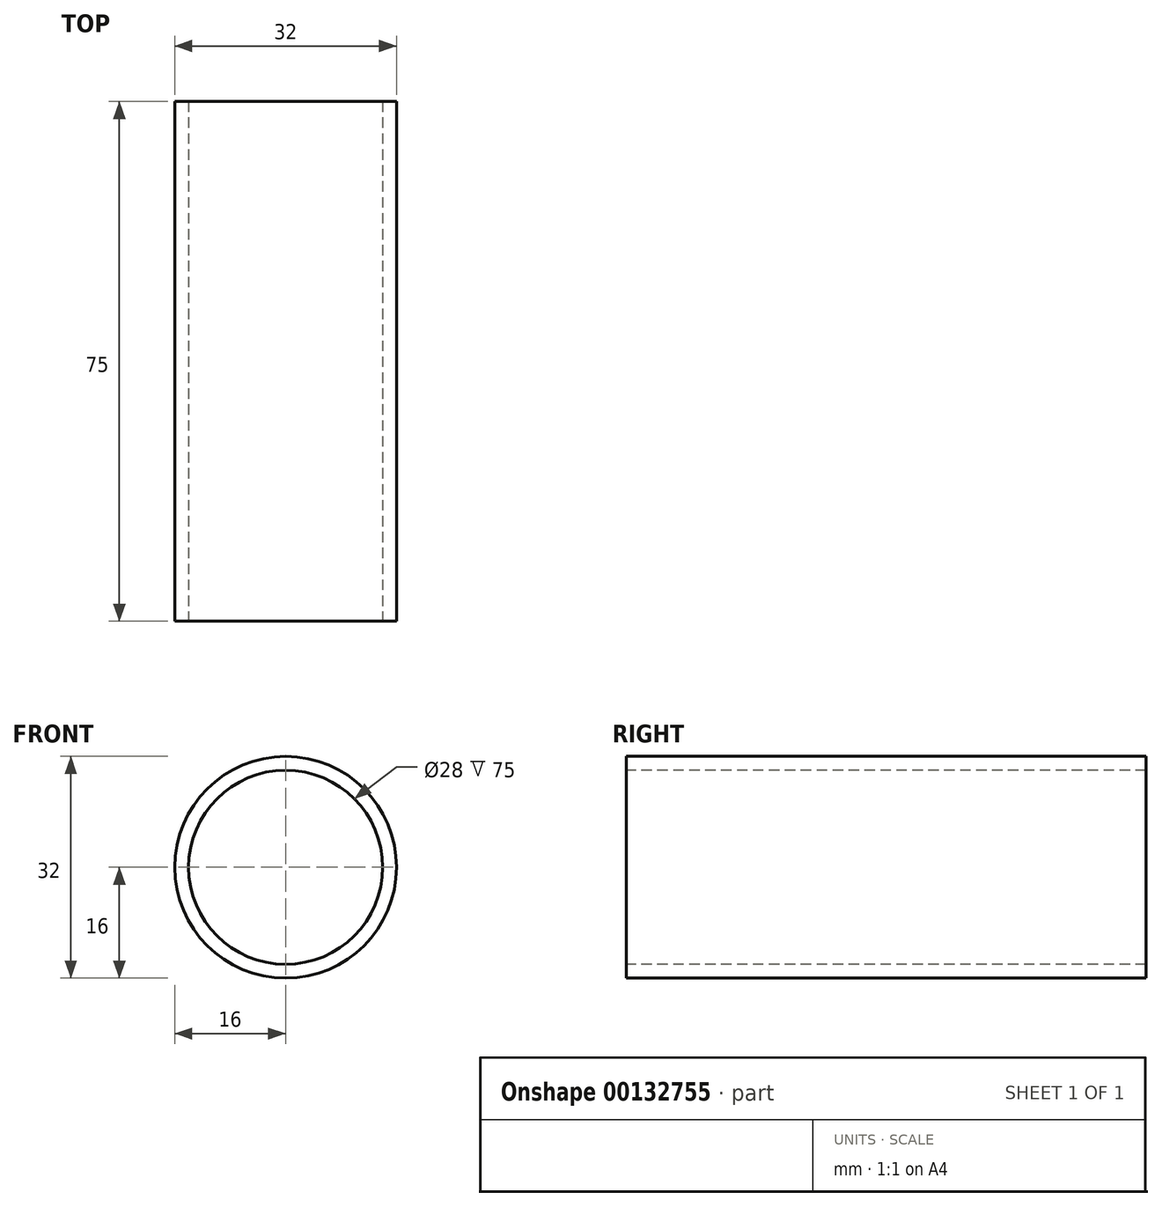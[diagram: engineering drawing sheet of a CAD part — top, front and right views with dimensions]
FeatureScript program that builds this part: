
annotation { "Feature Type Name" : "Feature", "Feature Type Description" : "" }
export const myFeature = defineFeature(function(context is Context, id is Id, definition is map)
    precondition{}
    {
        {
            var Q0;
            Q0=qCreatedBy(makeId("Front.planeOp"),FACE);
            var sketch = newSketch(context, id + "F0", { "sketchPlane" : qUnion([Q0])});
            skCircle(sketch, "E0", {"center": v(0, 0) * mm, "radius": 16 * mm});
            skCircle(sketch, "E1", {"center": v(0, 0) * mm, "radius": 14 * mm});
            skSolve(sketch);
        }
        {
            var Q0;
            Q0=makeQuery(id+"F0.imprint","IMPRINT",FACE,{"disambiguationData":[TD([[makeQuery(id+"F0.imprint","IMPRINT",EDGE,{"derivedFrom":sQuery(id+"F0.wireOp",EDGE,"E0")}),1.0]])]});
            extrude(context, id + "F1", {"entities" : qUnion([Q0]), "oppositeDirection" : true, "depth" : 75 * mm});
        }
    });
